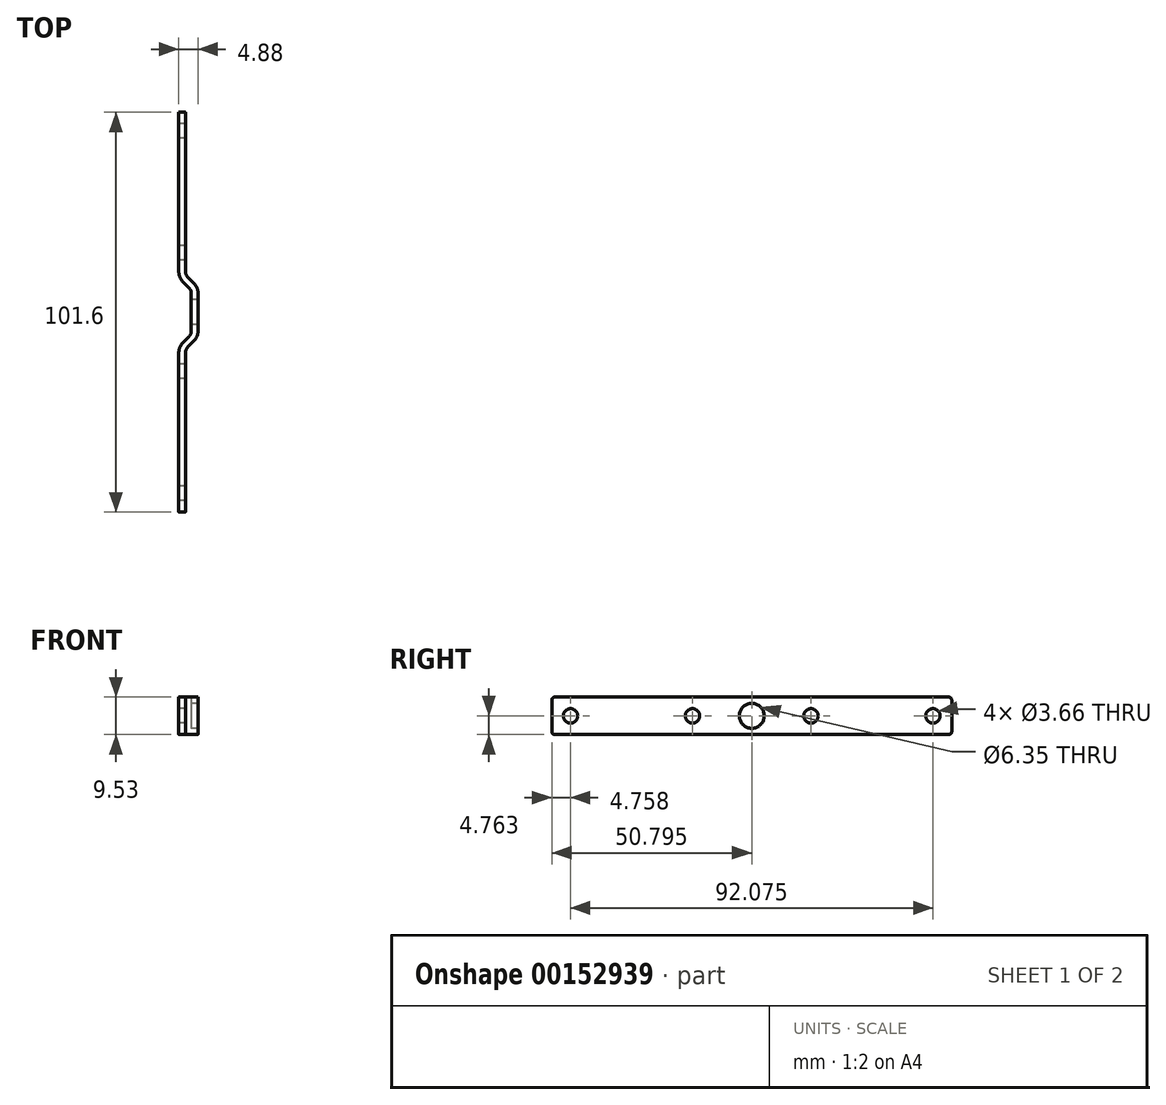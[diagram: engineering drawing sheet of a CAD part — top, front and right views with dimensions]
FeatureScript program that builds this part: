
annotation { "Feature Type Name" : "Feature", "Feature Type Description" : "" }
export const myFeature = defineFeature(function(context is Context, id is Id, definition is map)
    precondition{}
    {
        {
            var Q0;
            Q0=qCreatedBy(makeId("Top.planeOp"),FACE);
            var sketch = newSketch(context, id + "F0", { "sketchPlane" : qUnion([Q0])});
            skArc(sketch, "E0", {"start": v(0, 0) * mm, "mid": v(0.43, 0.64) * mm, "end": v(0.58, 1.4) * mm});
            skLineSegment(sketch, "E1", {"start": v(0, 0) * mm, "end": v(-1.51, -1.51) * mm});
            skArc(sketch, "E2", {"start": v(-1.51, -1.51) * mm, "mid": v(-2.31, -2.71) * mm, "end": v(-2.6, -4.12) * mm});
            skLineSegment(sketch, "E3", {"start": v(-2.6, -4.12) * mm, "end": v(-2.6, 16.45) * mm, "construction": true});
            skLineSegment(sketch, "E4", {"start": v(0.58, 1.4) * mm, "end": v(0.58, 10.93) * mm});
            skLineSegment(sketch, "E5", {"start": v(0.58, 6.17) * mm, "end": v(-2.6, 6.17) * mm, "construction": true});
            skLineSegment(sketch, "E6", {"start": v(-0.76, -0.76) * mm, "end": v(0.45, -1.96) * mm, "construction": true});
            skLineSegment(sketch, "E7", {"start": v(-0.3, -2.72) * mm, "end": v(1.2, -1.2) * mm});
            skArc(sketch, "E8", {"start": v(1.2, -1.2) * mm, "mid": v(2, -0.01) * mm, "end": v(2.3, 1.4) * mm});
            skArc(sketch, "E9", {"start": v(-0.3, -2.72) * mm, "mid": v(-0.73, -3.36) * mm, "end": v(-0.88, -4.12) * mm});
            skLineSegment(sketch, "E10", {"start": v(-2.6, -4.12) * mm, "end": v(-0.88, -4.12) * mm, "construction": true});
            skLineSegment(sketch, "E11", {"start": v(0.58, 1.4) * mm, "end": v(2.3, 1.4) * mm, "construction": true});
            skLineSegment(sketch, "E12", {"start": v(2.3, 1.4) * mm, "end": v(2.3, 10.93) * mm});
            skLineSegment(sketch, "E13", {"start": v(-2.6, -4.12) * mm, "end": v(-2.6, -44.63) * mm});
            skLineSegment(sketch, "E14", {"start": v(-0.88, -4.12) * mm, "end": v(-0.88, -44.63) * mm});
            skLineSegment(sketch, "E15", {"start": v(-0.88, -44.63) * mm, "end": v(-2.6, -44.63) * mm});
            skArc(sketch, "E16", {"start": v(-2.6, 16.45) * mm, "mid": v(-2.31, 15.04) * mm, "end": v(-1.51, 13.84) * mm});
            skArc(sketch, "E17", {"start": v(0.58, 10.93) * mm, "mid": v(0.43, 11.69) * mm, "end": v(0, 12.33) * mm});
            skLineSegment(sketch, "E18", {"start": v(-1.51, 13.84) * mm, "end": v(0, 12.33) * mm});
            skLineSegment(sketch, "E19", {"start": v(0.58, 10.93) * mm, "end": v(2.3, 10.93) * mm, "construction": true});
            skArc(sketch, "E20", {"start": v(2.3, 10.93) * mm, "mid": v(2, 12.34) * mm, "end": v(1.2, 13.54) * mm});
            skArc(sketch, "E21", {"start": v(-0.88, 16.45) * mm, "mid": v(-0.73, 15.7) * mm, "end": v(-0.3, 15.05) * mm});
            skLineSegment(sketch, "E22", {"start": v(1.2, 13.54) * mm, "end": v(-0.3, 15.05) * mm});
            skLineSegment(sketch, "E23", {"start": v(-2.6, 16.45) * mm, "end": v(-0.88, 16.45) * mm, "construction": true});
            skLineSegment(sketch, "E24", {"start": v(-2.6, 16.45) * mm, "end": v(-2.6, 56.97) * mm});
            skLineSegment(sketch, "E25", {"start": v(-2.6, 56.97) * mm, "end": v(-0.88, 56.97) * mm});
            skLineSegment(sketch, "E26", {"start": v(-0.88, 56.97) * mm, "end": v(-0.88, 16.45) * mm});
            skSolve(sketch);
        }
        {
            var Q0;
            Q0=qSketchRegion(id+"F0",true);
            extrude(context, id + "F1", {"entities" : qUnion([Q0]), "depth" : 9.52 * mm});
        }
        {
            var Q0;
            {var subQ0=sQuery(id+"F0.wireOp",EDGE,"E24");Q0=makeQuery(id+"FBPYhQcztcHPAAm_1.boolean.opBoolean","MERGE",FACE,{"derivedFrom":[makeQuery(id+"F1.opExtrude","SWEPT_FACE",FACE,{"disambiguationData":[OSD([subQ0])]}),makeQuery(id+"FBPYhQcztcHPAAm_1.opExtrude","SWEPT_FACE",FACE,{"disambiguationData":[OSD([subQ0])]})]});}
            var sketch = newSketch(context, id + "F2", { "sketchPlane" : qUnion([Q0])});
            skLineSegment(sketch, "E27.bottom", {"start": v(-56.97, 4.76) * mm, "end": v(-52.2, 4.76) * mm, "construction": true});
            skLineSegment(sketch, "E27.top", {"start": v(-56.97, 9.53) * mm, "end": v(-52.2, 9.53) * mm, "construction": true});
            skLineSegment(sketch, "E27.left", {"start": v(-56.97, 4.76) * mm, "end": v(-56.97, 9.53) * mm, "construction": true});
            skLineSegment(sketch, "E27.right", {"start": v(-52.2, 4.76) * mm, "end": v(-52.2, 9.53) * mm, "construction": true});
            skLineSegment(sketch, "E28.bottom", {"start": v(44.63, 4.76) * mm, "end": v(39.87, 4.76) * mm, "construction": true});
            skLineSegment(sketch, "E28.top", {"start": v(44.63, 9.53) * mm, "end": v(39.87, 9.53) * mm, "construction": true});
            skLineSegment(sketch, "E28.left", {"start": v(44.63, 4.76) * mm, "end": v(44.63, 9.53) * mm, "construction": true});
            skLineSegment(sketch, "E28.right", {"start": v(39.87, 4.76) * mm, "end": v(39.87, 9.52) * mm, "construction": true});
            skLineSegment(sketch, "E29", {"start": v(-16.45, 4.76) * mm, "end": v(-21.22, 4.76) * mm, "construction": true});
            skLineSegment(sketch, "E30", {"start": v(4.12, 4.76) * mm, "end": v(8.89, 4.76) * mm, "construction": true});
            skCircle(sketch, "E31", {"center": v(-52.2, 4.76) * mm, "radius": 1.83 * mm});
            skCircle(sketch, "E32", {"center": v(-21.22, 4.76) * mm, "radius": 1.83 * mm});
            skCircle(sketch, "E33", {"center": v(8.89, 4.76) * mm, "radius": 1.83 * mm});
            skCircle(sketch, "E34", {"center": v(39.87, 4.76) * mm, "radius": 1.83 * mm});
            skLineSegment(sketch, "E35", {"start": v(-16.45, 4.76) * mm, "end": v(4.12, 4.76) * mm, "construction": true});
            skCircle(sketch, "E36", {"center": v(-6.17, 4.76) * mm, "radius": 3.18 * mm});
            skSolve(sketch);
        }
        {
            var Q0;
            Q0=qSketchRegion(id+"F2",true);
            var Q1;
            Q1=makeQuery(id+"F1.opExtrude","SWEPT_FACE",FACE,{"disambiguationData":[OSD([sQuery(id+"F0.wireOp",EDGE,"E12")])]});
            extrude(context, id + "F3", {"entities" : qUnion([Q0]), "operationType" : NewBodyOperationType.REMOVE, "endBound" : BoundingType.UP_TO_SURFACE, "oppositeDirection" : true, "endBoundEntityFace" : qUnion([Q1]), "depth" : 25.4 * mm});
        }
        {
            var Q0;
            Q0=makeQuery(id+"F1.opExtrude","CAP_EDGE",EDGE,{"disambiguationData":[OSD([sQuery(id+"F0.wireOp",EDGE,"E25")])],"isStart":false});
            var Q1;
            Q1=makeQuery(id+"F1.opExtrude","CAP_EDGE",EDGE,{"disambiguationData":[OSD([sQuery(id+"F0.wireOp",EDGE,"E25")])],"isStart":true});
            var Q2;
            Q2=makeQuery(id+"F1.opExtrude","CAP_EDGE",EDGE,{"disambiguationData":[OSD([sQuery(id+"F0.wireOp",EDGE,"E15")])],"isStart":false});
            var Q3;
            Q3=makeQuery(id+"F1.opExtrude","CAP_EDGE",EDGE,{"disambiguationData":[OSD([sQuery(id+"F0.wireOp",EDGE,"E15")])],"isStart":true});
            fillet(context, id + "F4", {"entities" : qUnion([Q0, Q1, Q2, Q3]), "radius" : 0.76 * mm, "tangentPropagation" : true, "allowEdgeOverflow" : false});
        }
    });
